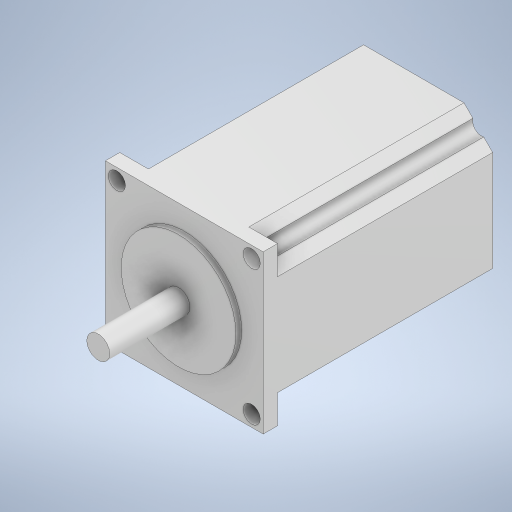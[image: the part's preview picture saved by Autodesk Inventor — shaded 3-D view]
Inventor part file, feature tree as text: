
AUTODESK INVENTOR PART (.ipt)
format: ipt  version: 2024 (Build 280153000, 153)  size: 312,320 bytes
history: native  units: mm
features: extrude x5, sketch x5, projected_geometry x3, chamfer x1
ambient origin geometry x8: Origin, YZ Plane, XZ Plane, XY Plane, X Axis, Y Axis, Z Axis, Center Point
bodies: Solid1 (feature_tree)
feature tree (14):
  extrude  "Extrusion1"  Depth=55.0mm
  extrude  "Extrusion2"  Depth=80.0mm
  extrude  "Extrusion3"  Depth=40.0mm
  chamfer  "Chamfer1"  Distance=2.0mm
  extrude  "Extrusion4"  Depth=10.0mm TaperAngle=45.0deg
  extrude  "Extrusion5"  Depth=5.0mm TaperAngle=0.0deg
  sketch  "Sketch1"  dims[d0=55.0mm d1=55.0mm]
  sketch  "Sketch2"  dims[d2=80.0mm d3=0.0mm d7=27.5mm]
  projected_geometry  "Projected Loop1"
  sketch  "Sketch3"  dims[d8=27.5mm d9=40.0mm]
  projected_geometry  "Projected Loop2"
  sketch  "Sketch4"  dims[d10=8.0mm d11=2.0mm d12=0.0mm]
  projected_geometry  "Projected Loop3"
  sketch  "Sketch5"  dims[d13=30.0mm d14=0.0mm d15=10.0mm d16=2.0mm d17=45.0deg d18=5.0mm d19=0.0mm d20=4.0mm d21=4.0mm d22=6.0mm d23=4.0mm d24=4.0mm d25=4.0mm d26=4.0mm d27=4.0mm d28=4.0mm d29=0.0mm d30=0.0mm]
